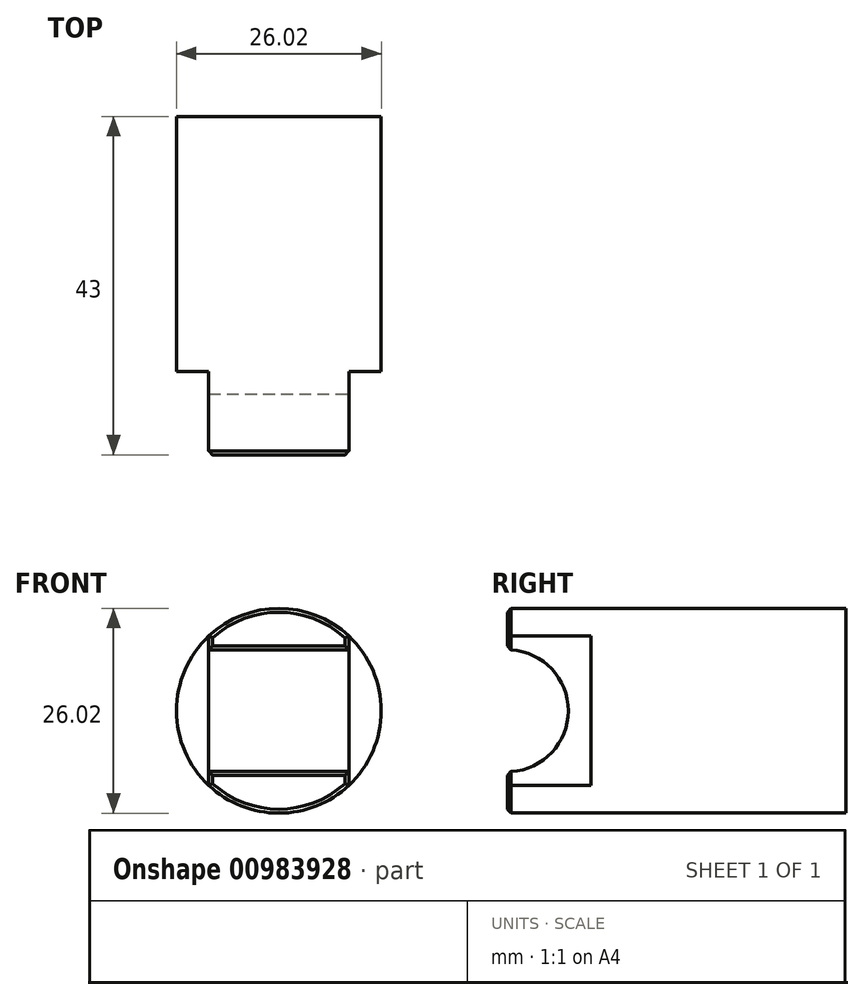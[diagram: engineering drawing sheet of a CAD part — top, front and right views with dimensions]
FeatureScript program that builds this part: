
annotation { "Feature Type Name" : "Feature", "Feature Type Description" : "" }
export const myFeature = defineFeature(function(context is Context, id is Id, definition is map)
    precondition{}
    {
        {
            var Q0;
            Q0=qCreatedBy(makeId("Front.planeOp"),FACE);
            var sketch = newSketch(context, id + "F0", { "sketchPlane" : qUnion([Q0])});
            skCircle(sketch, "E0", {"center": v(0, 0) * mm, "radius": 13 * mm});
            skSolve(sketch);
        }
        {
            var Q0;
            Q0 = qSketchRegion(id + "F0", true);
            extrude(context, id + "F1", {"entities" : qUnion([Q0]), "oppositeDirection" : true, "depth" : 43 * mm, "offsetDistance" : 25 * mm});
        }
        {
            var Q0;
            Q0=qCreatedBy(makeId("Right.planeOp"),FACE);
            var sketch = newSketch(context, id + "F2", { "sketchPlane" : qUnion([Q0])});
            skCircle(sketch, "E1", {"center": v(0, 0) * mm, "radius": 7.75 * mm});
            skSolve(sketch);
        }
        {
            var Q0;
            Q0 = qSketchRegion(id + "F2", true);
            extrude(context, id + "F3", {"entities" : qUnion([Q0]), "operationType" : NewBodyOperationType.REMOVE, "endBound" : BoundingType.THROUGH_ALL, "oppositeDirection" : true, "depth" : 25 * mm, "offsetDistance" : 25 * mm, "hasSecondDirection" : true, "secondDirectionOppositeDirection" : false, "secondDirectionDepth" : 25 * mm});
        }
        {
            var Q0;
            Q0=qCreatedBy(makeId("Top.planeOp"),FACE);
            var sketch = newSketch(context, id + "F4", { "sketchPlane" : qUnion([Q0])});
            skLineSegment(sketch, "E2.bottom", {"start": v(8.9, 10.6) * mm, "end": v(16.08, 10.6) * mm});
            skLineSegment(sketch, "E2.top", {"start": v(8.9, -1.9) * mm, "end": v(16.08, -1.9) * mm});
            skLineSegment(sketch, "E2.left", {"start": v(8.9, 10.6) * mm, "end": v(8.9, -1.9) * mm});
            skLineSegment(sketch, "E2.right", {"start": v(16.08, 10.6) * mm, "end": v(16.08, -1.9) * mm});
            skLineSegment(sketch, "E3.MirrorCS", {"start": v(-16.08, 10.6) * mm, "end": v(-16.08, -1.9) * mm});
            skLineSegment(sketch, "E4.MirrorCS", {"start": v(-8.9, 10.6) * mm, "end": v(-8.9, -1.9) * mm});
            skLineSegment(sketch, "E5.MirrorCS", {"start": v(-8.9, -1.9) * mm, "end": v(-16.08, -1.9) * mm});
            skLineSegment(sketch, "E6.MirrorCS", {"start": v(-8.9, 10.6) * mm, "end": v(-16.08, 10.6) * mm});
            skSolve(sketch);
        }
        {
            var Q0;
            Q0 = qSketchRegion(id + "F4", true);
            extrude(context, id + "F5", {"entities" : qUnion([Q0]), "operationType" : NewBodyOperationType.REMOVE, "endBound" : BoundingType.SYMMETRIC, "oppositeDirection" : true, "depth" : 25 * mm, "offsetDistance" : 25 * mm});
        }
        {
            var Q0;
            Q0=makeQuery(id+"F3.boolean.opBoolean","SPLIT",FACE,{"disambiguationData":[OD(1.0)],"derivedFrom":makeQuery(id+"F1.opExtrude","CAP_FACE",FACE,{"disambiguationData":[OSD([sQuery(id+"F0.wireOp",EDGE,"E0")])],"isStart":true})});
            var Q1;
            Q1=makeQuery(id+"F3.boolean.opBoolean","SPLIT",FACE,{"disambiguationData":[OD(0.0)],"derivedFrom":makeQuery(id+"F1.opExtrude","CAP_FACE",FACE,{"disambiguationData":[OSD([sQuery(id+"F0.wireOp",EDGE,"E0")])],"isStart":true})});
            chamfer(context, id + "F6", {"entities" : qUnion([Q0, Q1]), "width" : .5 * mm, "tangentPropagation" : true});
        }
    });
